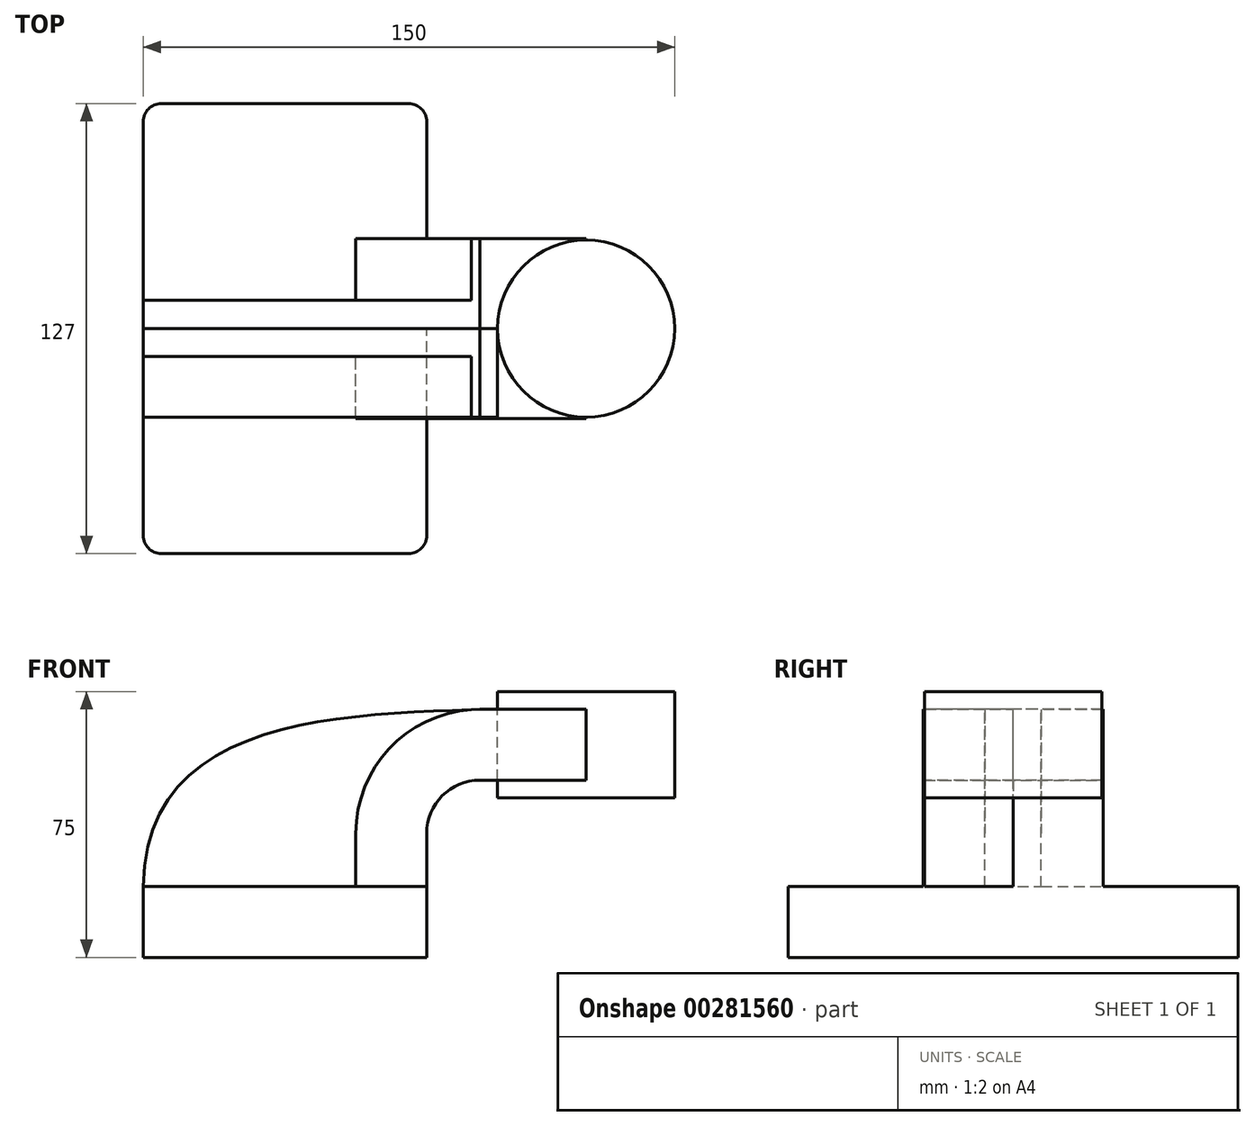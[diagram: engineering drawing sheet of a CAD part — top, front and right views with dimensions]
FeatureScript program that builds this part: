
annotation { "Feature Type Name" : "Feature", "Feature Type Description" : "" }
export const myFeature = defineFeature(function(context is Context, id is Id, definition is map)
    precondition{}
    {
        {
            var Q0;
            Q0=qCreatedBy(makeId("Front.planeOp"),FACE);
            var sketch = newSketch(context, id + "F0", { "sketchPlane" : qUnion([Q0])});
            skLineSegment(sketch, "E0.rect.bottom", {"start": v(-40, 10) * mm, "end": v(40, 10) * mm});
            skLineSegment(sketch, "E0.rect.top", {"start": v(-40, -10) * mm, "end": v(40, -10) * mm});
            skLineSegment(sketch, "E0.rect.left", {"start": v(-40, 10) * mm, "end": v(-40, -10) * mm});
            skLineSegment(sketch, "E0.rect.right", {"start": v(40, 10) * mm, "end": v(40, -10) * mm});
            skPoint(sketch, "E0.rect.middle", {"position": v(0, 0) * mm});
            skLineSegment(sketch, "E1", {"start": v(40, 10) * mm, "end": v(40, 25) * mm});
            skArc(sketch, "E2", {"start": v(40, 25) * mm, "mid": v(44.4, 35.6) * mm, "end": v(55, 40) * mm});
            skLineSegment(sketch, "E3", {"start": v(55, 40) * mm, "end": v(85, 40) * mm});
            skLineSegment(sketch, "E4.rect.bottom", {"start": v(60, 35) * mm, "end": v(110, 35) * mm});
            skLineSegment(sketch, "E4.rect.top", {"start": v(60, 65) * mm, "end": v(110, 65) * mm});
            skLineSegment(sketch, "E4.rect.left", {"start": v(60, 35) * mm, "end": v(60, 65) * mm});
            skLineSegment(sketch, "E4.rect.right", {"start": v(110, 35) * mm, "end": v(110, 65) * mm});
            skPoint(sketch, "E4.rect.middle", {"position": v(85, 50) * mm});
            skLineSegment(sketch, "E5.0", {"start": v(55, 60) * mm, "end": v(85, 60) * mm});
            skArc(sketch, "E5.1", {"start": v(20, 25) * mm, "mid": v(30.25, 49.75) * mm, "end": v(55, 60) * mm});
            skLineSegment(sketch, "E5.2", {"start": v(20, 10) * mm, "end": v(20, 25) * mm});
            skLineSegment(sketch, "E6", {"start": v(85, 35) * mm, "end": v(85, 65) * mm});
            skFitSpline(sketch, "E7", {"points": [v(-40, 10) * mm, v(55, 60) * mm], "startDerivative": vector(1.75, 142.89) * mm, "endDerivative": vector(120.92, 4.22) * mm});
            skSolve(sketch);
        }
        {
            var Q0;
            Q0=makeQuery(id+"F0.imprint","IMPRINT",FACE,{"disambiguationData":[TD([[makeQuery(id+"F0.imprint","IMPRINT",EDGE,{"derivedFrom":sQuery(id+"F0.wireOp",EDGE,"E0.rect.top")}),1.0]])]});
            extrude(context, id + "F1", {"entities" : qUnion([Q0]), "endBound" : BoundingType.SYMMETRIC, "depth" : 127 * mm});
        }
        {
            var Q0;
            {var subQ9=sQuery(id+"F0.wireOp",EDGE,"E1");Q0=makeQuery(id+"F0.imprint","IMPRINT",FACE,{"disambiguationData":[TD([[makeQuery(id+"F0.imprint","IMPRINT",EDGE,{"derivedFrom":subQ9}),1.0]])]});}
            var Q1;
            {var subQ0=sQuery(id+"F0.wireOp",EDGE,"E6");var subQ1=sQuery(id+"F0.wireOp",EDGE,"E3");var subQ2=makeQuery(id+"F0.imprint","INTERSECT",VERTEX,{"derivedFrom":[subQ1,subQ0]});Q1=makeQuery(id+"F0.imprint","IMPRINT",FACE,{"disambiguationData":[TD([[makeQuery(id+"F0.imprint","IMPRINT",EDGE,{"disambiguationData":[TD([[subQ2,1.0]])],"derivedFrom":subQ1}),1.0]])]});}
            extrude(context, id + "F2", {"entities" : qUnion([Q0, Q1]), "operationType" : NewBodyOperationType.ADD, "endBound" : BoundingType.SYMMETRIC, "depth" : 50.8 * mm});
        }
        {
            var Q0;
            {var subQ3=sQuery(id+"F0.wireOp",EDGE,"E5.2");Q0=makeQuery(id+"F0.imprint","IMPRINT",FACE,{"disambiguationData":[TD([[makeQuery(id+"F0.imprint","IMPRINT",EDGE,{"derivedFrom":subQ3}),1.0]])]});}
            extrude(context, id + "F3", {"entities" : qUnion([Q0]), "operationType" : NewBodyOperationType.ADD, "endBound" : BoundingType.SYMMETRIC, "depth" : 15.88 * mm});
        }
        {
            var Q0;
            {var subQ5=sQuery(id+"F0.wireOp",EDGE,"E4.rect.right");Q0=makeQuery(id+"F0.imprint","IMPRINT",FACE,{"disambiguationData":[TD([[makeQuery(id+"F0.imprint","IMPRINT",EDGE,{"derivedFrom":subQ5}),1.0]])]});}
            var Q1;
            Q1=sQuery(id+"F0.wireOp",EDGE,"E6");
            revolve(context, id + "F4", {"operationType" : NewBodyOperationType.ADD, "entities" : qUnion([Q0]), "axis" : qUnion([Q1]), "revolveType" : RevolveType.FULL});
        }
        {
            var Q0;
            Q0=makeQuery(id+"F1.opExtrude","CAP_EDGE",EDGE,{"disambiguationData":[OSD([sQuery(id+"F0.wireOp",EDGE,"E0.rect.right")])],"isStart":false});
            var Q1;
            Q1=makeQuery(id+"F1.opExtrude","CAP_EDGE",EDGE,{"disambiguationData":[OSD([sQuery(id+"F0.wireOp",EDGE,"E0.rect.left")])],"isStart":false});
            var Q2;
            Q2=makeQuery(id+"F1.opExtrude","CAP_EDGE",EDGE,{"disambiguationData":[OSD([sQuery(id+"F0.wireOp",EDGE,"E0.rect.right")])],"isStart":true});
            var Q3;
            Q3=makeQuery(id+"F1.opExtrude","CAP_EDGE",EDGE,{"disambiguationData":[OSD([sQuery(id+"F0.wireOp",EDGE,"E0.rect.left")])],"isStart":true});
            fillet(context, id + "F5", {"entities" : qUnion([Q0, Q1, Q2, Q3]), "radius" : 5.08 * mm, "tangentPropagation" : true, "allowEdgeOverflow" : false});
        }
        {
            var Q0;
            {var subQ4=sQuery(id+"F0.wireOp",EDGE,"E1");Q0=makeQuery(id+"F0.imprint","IMPRINT",FACE,{"disambiguationData":[TD([[makeQuery(id+"F0.imprint","IMPRINT",EDGE,{"derivedFrom":subQ4}),1.0]])]});}
            var Q1;
            {var subQ3=sQuery(id+"F0.wireOp",EDGE,"E5.2");Q1=makeQuery(id+"F0.imprint","IMPRINT",FACE,{"disambiguationData":[TD([[makeQuery(id+"F0.imprint","IMPRINT",EDGE,{"derivedFrom":subQ3}),1.0]])]});}
            extrude(context, id + "F6", {"entities" : qUnion([Q0, Q1]), "depth" : 25 * mm});
        }
    });
